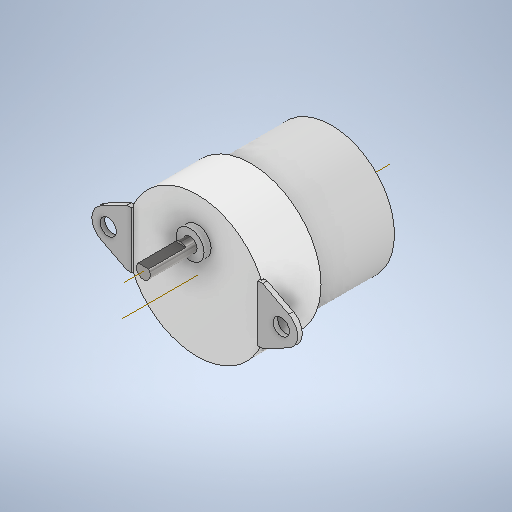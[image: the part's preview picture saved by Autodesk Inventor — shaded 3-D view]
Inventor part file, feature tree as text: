
AUTODESK INVENTOR PART (.ipt)
format: ipt  version: 2025.3 (Build 293356030, 356C)  size: 332,288 bytes
history: native  units: mm
features: extrude x8, sketch x8, other x6
ambient origin geometry x8: Origin, YZ Plane, XZ Plane, XY Plane, X Axis, Y Axis, Z Axis, Center Point
bodies: Body1 (feature_tree)
feature tree (22):
  other  "ソリッド1"
  extrude  "押し出し1"  Depth=30.0mm
  extrude  "押し出し2"  Depth=11.5mm TaperAngle=0.0deg
  extrude  "押し出し3"  Depth=6.0mm
  extrude  "押し出し4"  Depth=6.5mm
  extrude  "押し出し6"  Depth=1.5mm TaperAngle=0.0deg
  other  "作業平面1"
  extrude  "押し出し7"  Depth=3.0mm
  other  "作業平面3"
  extrude  "押し出し8"  Depth=10.0mm TaperAngle=0.0deg
  extrude  "押し出し9"  Depth=27.0mm
  other  "作業軸2"
  sketch  "スケッチ1"
  sketch  "スケッチ2"
  sketch  "スケッチ3"
  sketch  "スケッチ4"
  sketch  "スケッチ6"
  sketch  "スケッチ7"
  other  "作業軸1"
  other  "作業平面2"
  sketch  "スケッチ9"
  sketch  "スケッチ10"
